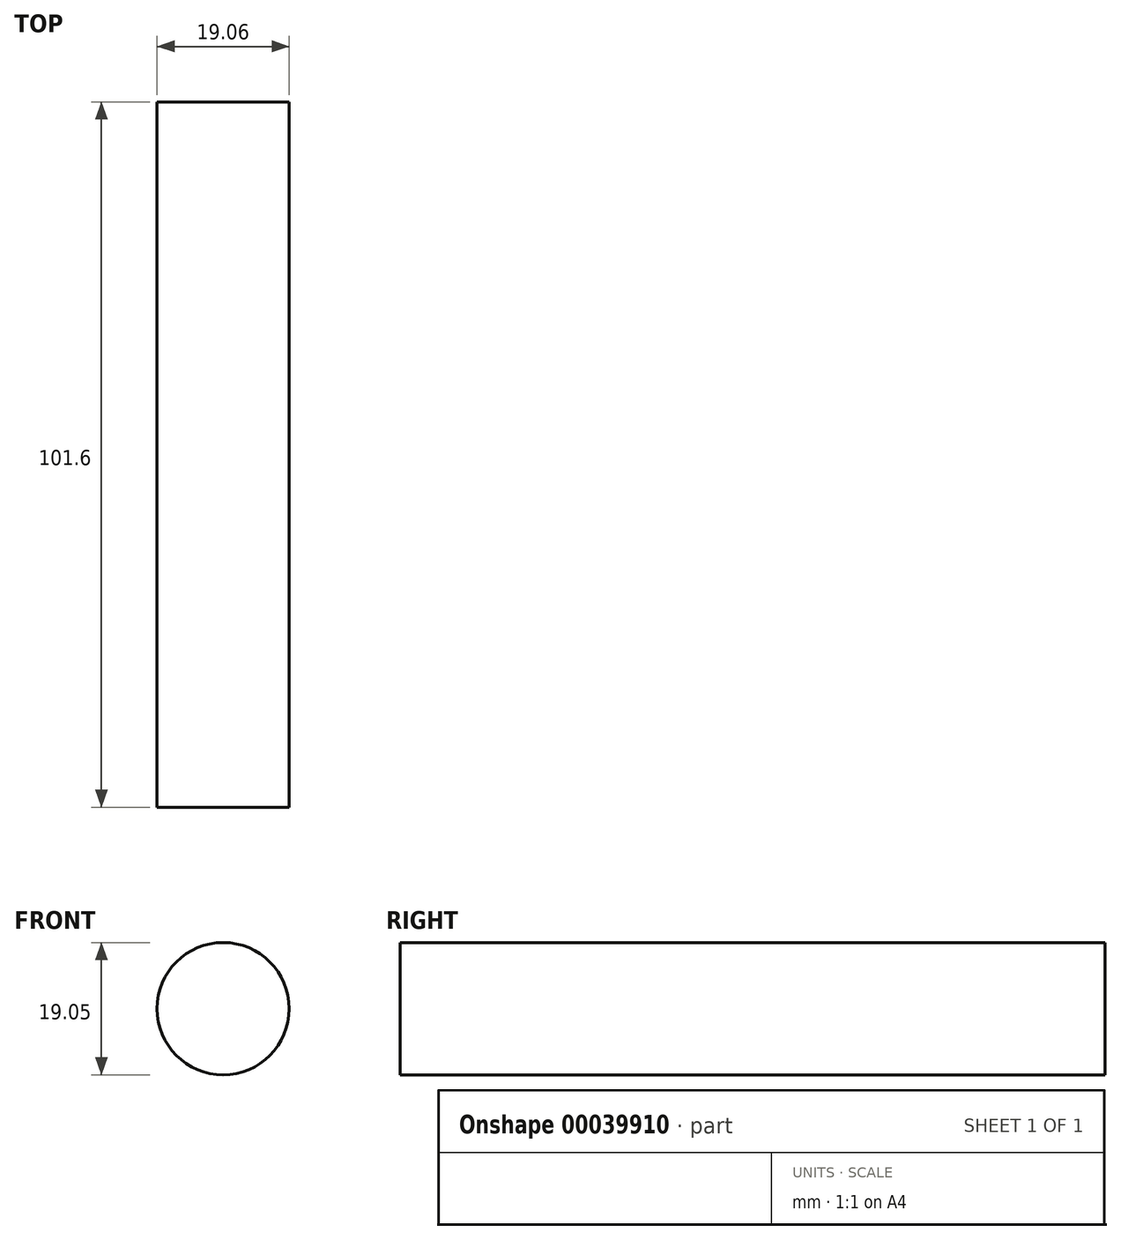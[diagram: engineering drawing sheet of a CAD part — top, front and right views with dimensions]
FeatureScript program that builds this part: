
annotation { "Feature Type Name" : "Feature", "Feature Type Description" : "" }
export const myFeature = defineFeature(function(context is Context, id is Id, definition is map)
    precondition{}
    {
        {
            var Q0;
            Q0=qCreatedBy(makeId("Front.planeOp"),FACE);
            var sketch = newSketch(context, id + "F0", { "sketchPlane" : qUnion([Q0])});
            skCircle(sketch, "E0", {"center": v(0, -0.97) * mm, "radius": 9.53 * mm});
            skSolve(sketch);
        }
        {
            var Q0;
            Q0 = qSketchRegion(id + "F0", true);
            extrude(context, id + "F1", {"entities" : qUnion([Q0]), "depth" : 101.6 * mm});
        }
    });
